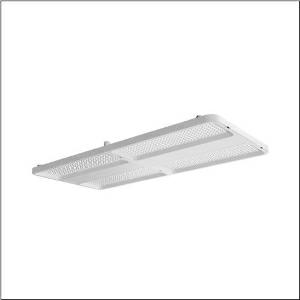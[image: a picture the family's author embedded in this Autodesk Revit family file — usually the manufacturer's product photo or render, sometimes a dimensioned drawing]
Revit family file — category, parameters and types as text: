
# Revit family: highbay_21_maxi_52hn12db4tda
name_source: partatom
category: Lighting Fixtures
units: mm (PartAtom-declared; Revit-internal decimal feet)

## family parameters
Cut with Voids When Loaded = No
Host = Face
Light Source = No
Part Type = Normal
Room Calculation Point = No
Round Connector Dimension = Use Diameter
Shared = No

## types (1)
- --- (1 x LED, 8350 lm, 44.8 W, 4000K)
    Apparent Load = 45 VA
    CIE Flux Codes = 90 98 100 100 100
    Color Rendering = 80
    Color Temperature = 4000K
    Default Elevation = 1800 mm
    Description = high bay luminaire Highbay 21 maxi; direct symmetric wide distribution, light control with lens of PMMA; UGR ≤ 22 (X = 4H | Y = 8H | S = 0.25H | reflection values 70/50/20); luminous flux: 53.000lm; light colour: 840, colour temperature: 4000K, MacAdam ≤ 3 SDCM (initial), colour rendering: CRI > 80; luminous efficacy: 184,9lm/W; rated service life: 75.000h (L80) at AT= ta max; control: DALI 2; luminaire connection: terminal, 5-pole, max. 2.5mm² (cable entry for one cable, Ø 8.5..16mm); mains connection: 230..240V, AC/DC 0/50..60Hz; connected load: 286,6W; protection rating (complete): IP66; insulation class (complete): insulation class I (protective earthing); protection symbol: D; impact resistance: IK08; certification: CE, ENEC, VDE, UKCA; luminaire for central battery installations according to EN 60598-2-22, internal wiring halogen-free; luminaire LABS conformity tested according to VDMA 24364:2018-05; Suitable for use in the food industry according to the specifications of IFS-Food, HACCP and/or BRC; housing frame of high-performance plastic PA6, matt traffic white (RAL 9016); cover of PMMA; dimension (LxWxH): 946 x 442 x 72mm; permissible operating ambient temperature: -40..+55°C (reducing of maximum allowable ambient temperature of 5°C with ceiling mounting); packaging unit: 1 piece; (delivery without accessories; please order mounting accessories separately)
    Height = 72 mm  [stored 0.23622 ft]
    Lamp = 1 x LED
    Lamp Light Flux = 8350 lm
    Lamp Power = 44.8 W
    Lamp count = 1
    Length = 946 mm
    Luminous efficacy = 186 lm/W
    Manufacturer = Siteco
    ModVariant = No
    Model = 52HN12DB4TDA
    Mounting Place = Ceiling
    Mounting Type = Pendant
    Number of Poles = 1
    OnlyDefault = Yes
    Power Factor = 1
    Product Name = Highbay 21 maxi
    Product group = high bay luminaire
    ProductGroupID = 902
    Protection Class = Protection class I
    Protection Degree = IP 66
    RLX_Detail_Level = 1
    RLX_Emergency_Light_Flux = 0 lm
    RLX_Emergency_Type = 0
    RLX_Emergency_Type_DB = No
    RlxData = <blob elided: 128421 chars, md5=bbb48bb2>
    Socket = socket
    Standby Power = 0 W
    System Light Flux = 8350 lm
    System Power = 45 W
    Type Comments = : DC mode (central or group accumulator) initial emergency light level
    Type Image = l_1363244.jpg
    URL = http://relux.com
    VarID = @adj_017709
    Voltage = 0 V
    Weight = 0.00 kg
    Width = 442 mm

note: [stored X ft] marks values corroborated as IEEE doubles in the binary element streams (Revit-internal decimal feet)

## geometry (parser evidence)
native form markers: Blend x4, Sweep x10
no freeform markers — native parametric forms only
